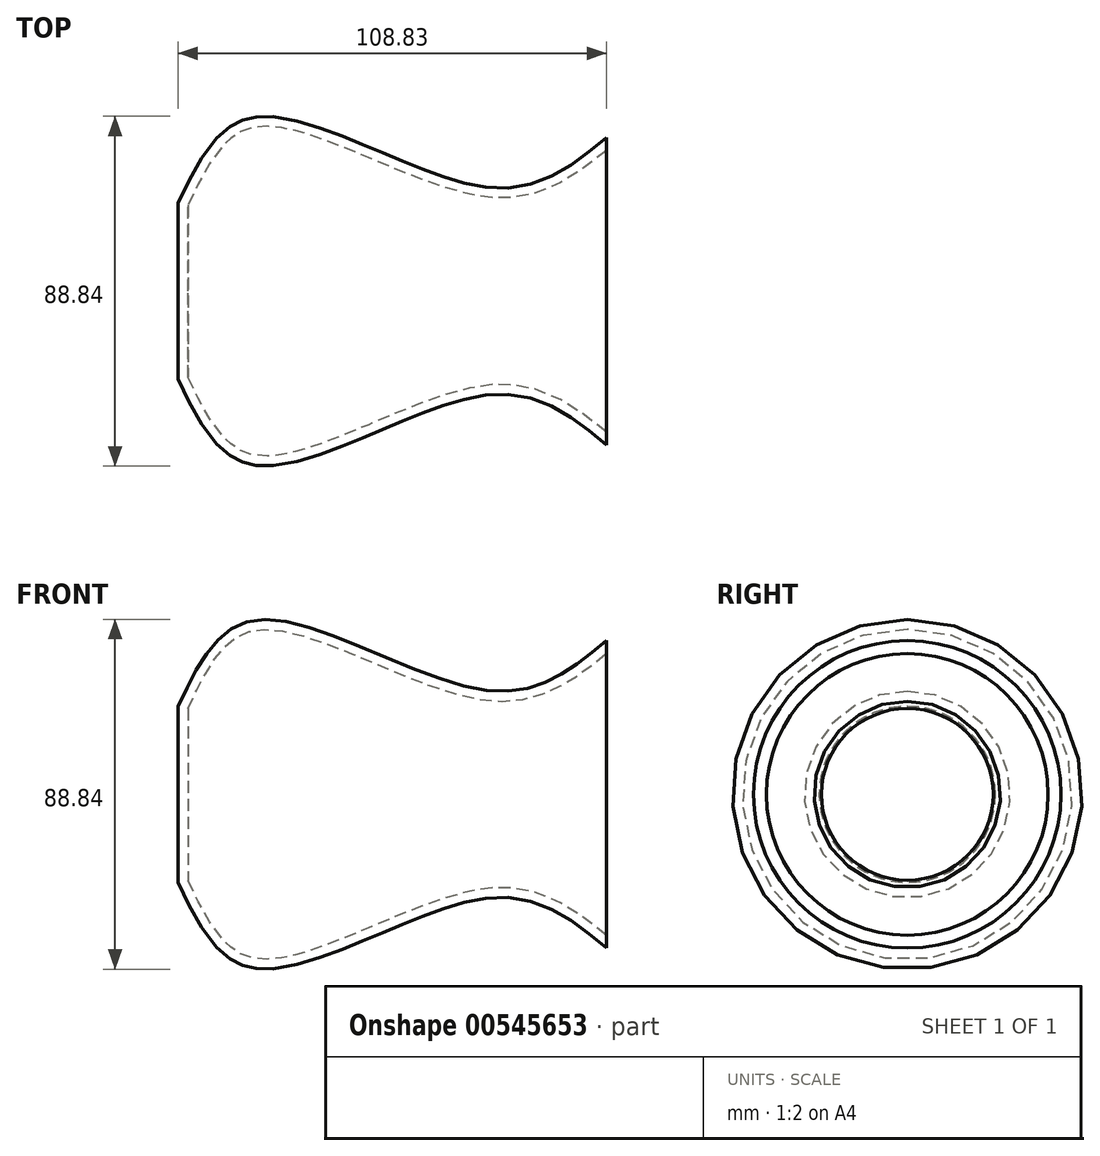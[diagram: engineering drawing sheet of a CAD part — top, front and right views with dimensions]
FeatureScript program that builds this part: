
annotation { "Feature Type Name" : "Feature", "Feature Type Description" : "" }
export const myFeature = defineFeature(function(context is Context, id is Id, definition is map)
    precondition{}
    {
        {
            var Q0;
            Q0=qCreatedBy(makeId("Front.planeOp"),FACE);
            var sketch = newSketch(context, id + "F0", { "sketchPlane" : qUnion([Q0])});
            skFitSpline(sketch, "E0", {"points": [v(-56.6, 22.38) * mm, v(-36.42, 44.32) * mm, v(22.38, 26.33) * mm, v(52.22, 39.05) * mm], "startDerivative": vector(51.23, 108.84) * mm, "endDerivative": vector(84.76, 70.36) * mm});
            skLineSegment(sketch, "E1", {"start": v(-56.6, 22.38) * mm, "end": v(-56.6, 0) * mm});
            skLineSegment(sketch, "E2", {"start": v(-56.6, 0) * mm, "end": v(51.78, 0) * mm});
            skLineSegment(sketch, "E3", {"start": v(51.78, 0) * mm, "end": v(52.22, 39.05) * mm});
            skSolve(sketch);
        }
        {
            var Q0;
            Q0=makeQuery(id+"F0.imprint","IMPRINT",FACE,{"disambiguationData":[TD([[makeQuery(id+"F0.imprint","IMPRINT",EDGE,{"derivedFrom":sQuery(id+"F0.wireOp",EDGE,"E0")}),-1.0]])]});
            var Q1;
            Q1=sQuery(id+"F0.wireOp",EDGE,"E2");
            revolve(context, id + "F1", {"entities" : qUnion([Q0]), "axis" : qUnion([Q1]), "revolveType" : RevolveType.FULL});
        }
        {
            var Q0;
            Q0=makeQuery(id+"F1.opRevolve","SWEPT_FACE",FACE,{"disambiguationData":[OSD([sQuery(id+"F0.wireOp",EDGE,"E3")])]});
            shell(context, id + "F2", {"entities" : qUnion([Q0]), "thickness" : 2.5 * mm});
        }
    });
